# Revit family: Prises non verrouilllées 20_25 V
name_source: partatom
category: Installations électriques
revit_build: Autodesk Revit 2018 (Build: 20170223_1515(x64)
units: mm (PartAtom-declared; Revit-internal decimal feet)

## family parameters
Conserver l'orientation des annotations = Non
Cote de connecteur circulaire = Utiliser le diamètre
Couper avec des vides une fois chargée = Non
Hôte = Face
Partagée = Non
Point de calcul de pièce = Non
Type d'élément = Normal

## types (2) — shared parameters
Couleur caractéristique = violet
Elévation par défaut = 1000 mm  [stored 3.28084 ft]
Fabricant = Legrand
Famille produit = 0854-P17 TEMPRA PRO
Nombre de pôles = 2
Prise au standard international pour montage encastré ou saillie avec accessoire permet la connexion d'appareils de puissance = Prise au standard international pour montage encastré ou saillie avec accessoire permet la connexion d'appareils de puissance
Standard CEI ou NFC = CEI
Température maximum d'utilisation = 40
Température minimum d'utilisation = -25
Tension V = 20 25 V  50/60 Hz  violet
classe de protection IP = IP44
entraxe de fixation horizontal mm = 70 mm
entraxe de fixation vertical mm = 70 mm
hauteur mm = 84 mm
installation Encastrée E ou Saillie S = encastré et saillie
largeur mm = 84 mm
matériau du boitier = plastique
profondeur d'encastrement mm = 33 mm  [stored 0.108268 ft]
profondeur mm = 66 mm
résistance aux chocs IK = 9
sans halogène = Oui
type de raccordement = bornes à vis
zero-valued in all types: Position de la Terre h

## per-type parameters (varying)
| type | Description | Intensité A |
| P17 - IP44 - 32A - 2P | LG-055295_Montage panneau prise P17 - IP 44 - 20/25 V - 32 A - 2P | 32 A |
| P17 - IP44 - 16 A - 2P | LG-055245_ P17 - IP 44 - 20/25 V - 16 A - 2P | 16 A |

note: [stored X ft] marks values corroborated as IEEE doubles in the binary element streams (Revit-internal decimal feet)
